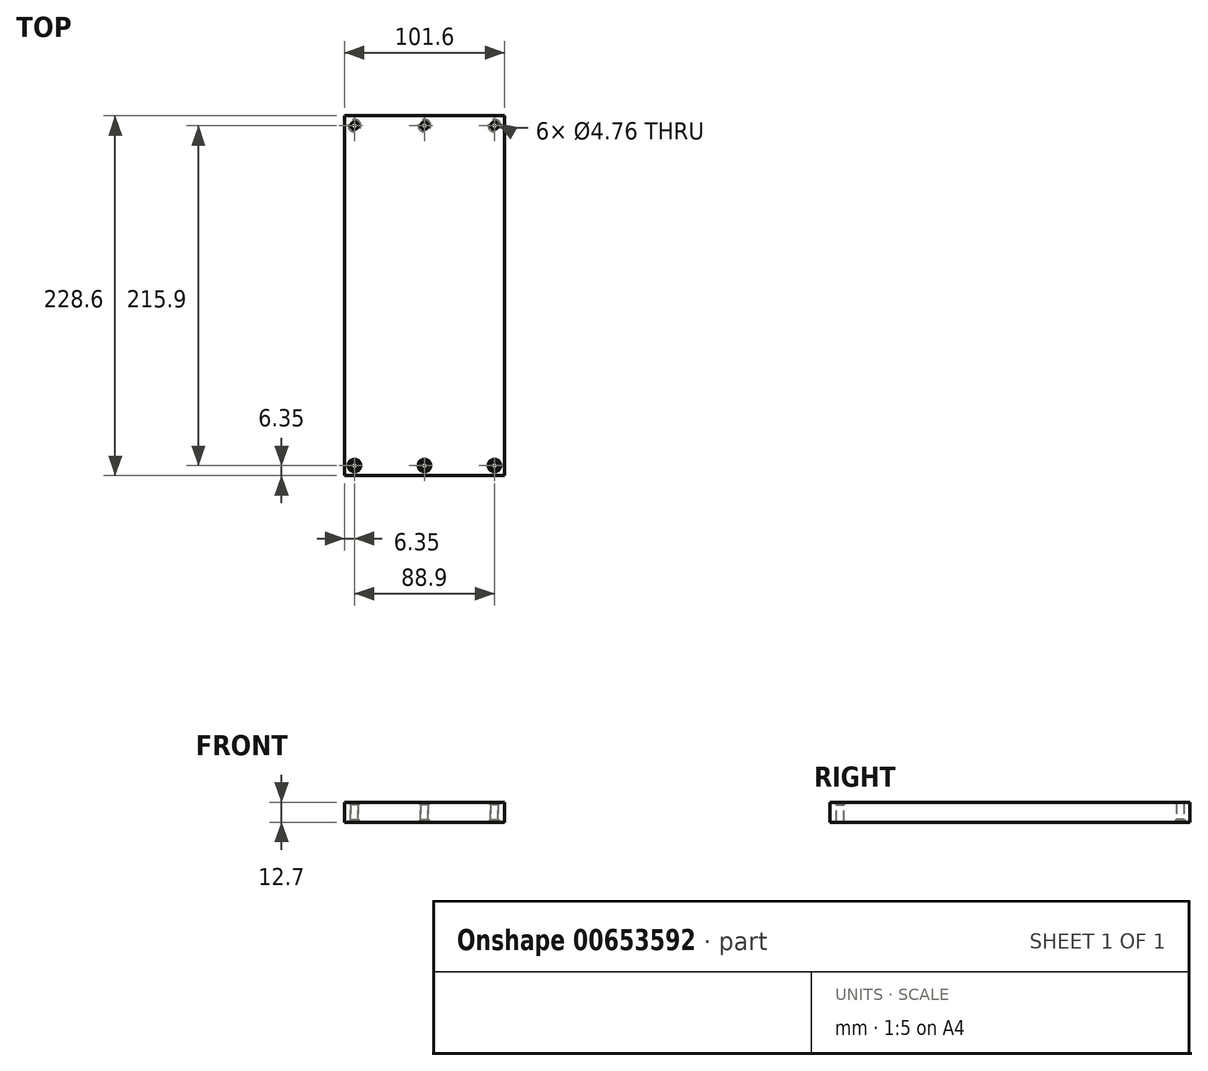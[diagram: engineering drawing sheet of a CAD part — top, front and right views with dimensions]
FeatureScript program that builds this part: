
annotation { "Feature Type Name" : "Feature", "Feature Type Description" : "" }
export const myFeature = defineFeature(function(context is Context, id is Id, definition is map)
    precondition{}
    {
        {
            var Q0;
            Q0=qCreatedBy(makeId("Top.planeOp"),FACE);
            var sketch = newSketch(context, id + "F0", { "sketchPlane" : qUnion([Q0])});
            skLineSegment(sketch, "E0.bottom", {"start": v(50.8, 114.3) * mm, "end": v(-50.8, 114.3) * mm});
            skLineSegment(sketch, "E0.top", {"start": v(50.8, -114.3) * mm, "end": v(-50.8, -114.3) * mm});
            skLineSegment(sketch, "E0.left", {"start": v(50.8, 114.3) * mm, "end": v(50.8, -114.3) * mm});
            skLineSegment(sketch, "E0.right", {"start": v(-50.8, 114.3) * mm, "end": v(-50.8, -114.3) * mm});
            skPoint(sketch, "E0.middle", {"position": v(0, 0) * mm});
            skSolve(sketch);
        }
        {
            var Q0;
            Q0=makeQuery(id+"F0.imprint","IMPRINT",FACE,{"disambiguationData":[TD([[makeQuery(id+"F0.imprint","IMPRINT",EDGE,{"derivedFrom":sQuery(id+"F0.wireOp",EDGE,"E0.bottom")}),1.0]])]});
            extrude(context, id + "F1", {"entities" : qUnion([Q0]), "depth" : 12.7 * mm, "offsetDistance" : 25.4 * mm});
        }
        {
            var Q0;
            Q0=makeQuery(id+"F1.opExtrude","CAP_FACE",FACE,{"disambiguationData":[OSD([sQuery(id+"F0.wireOp",EDGE,"E0.bottom"),sQuery(id+"F0.wireOp",EDGE,"E0.top"),sQuery(id+"F0.wireOp",EDGE,"E0.left"),sQuery(id+"F0.wireOp",EDGE,"E0.right")])],"isStart":false});
            var sketch = newSketch(context, id + "F2", { "sketchPlane" : qUnion([Q0])});
            skLineSegment(sketch, "E1.0", {"start": v(-44.45, -107.95) * mm, "end": v(44.45, -107.95) * mm});
            skLineSegment(sketch, "E1.1", {"start": v(-44.45, 107.95) * mm, "end": v(-44.45, -107.95) * mm});
            skLineSegment(sketch, "E1.2", {"start": v(44.45, 107.95) * mm, "end": v(-44.45, 107.95) * mm});
            skLineSegment(sketch, "E1.3", {"start": v(44.45, -107.95) * mm, "end": v(44.45, 107.95) * mm});
            skLineSegment(sketch, "E2", {"start": v(-44.45, -95.25) * mm, "end": v(44.45, -95.25) * mm});
            skLineSegment(sketch, "E3", {"start": v(44.45, 95.25) * mm, "end": v(-44.45, 95.25) * mm});
            skLineSegment(sketch, "E4", {"start": v(76.94, 0) * mm, "end": v(-80.05, 0) * mm, "construction": true});
            skPoint(sketch, "E5", {"position": v(0, 107.95) * mm});
            skPoint(sketch, "E6", {"position": v(14.82, 95.25) * mm});
            skPoint(sketch, "E7", {"position": v(-14.82, 95.25) * mm});
            skPoint(sketch, "E8", {"position": v(0, -107.95) * mm});
            skPoint(sketch, "E9", {"position": v(14.82, -95.25) * mm});
            skPoint(sketch, "E10", {"position": v(-14.82, -95.25) * mm});
            skLineSegment(sketch, "E11", {"start": v(-44.45, 95.25) * mm, "end": v(-14.82, 95.25) * mm, "construction": true});
            skLineSegment(sketch, "E12", {"start": v(-14.82, 95.25) * mm, "end": v(14.82, 95.25) * mm, "construction": true});
            skLineSegment(sketch, "E13", {"start": v(14.82, 95.25) * mm, "end": v(44.45, 95.25) * mm, "construction": true});
            skSolve(sketch);
        }
        {
            var Q0;
            Q0=sQuery(id+"F2.wireOp",VERTEX,"E1.1.end");
            var Q1;
            Q1=sQuery(id+"F2.wireOp",VERTEX,"E8");
            var Q2;
            Q2=sQuery(id+"F2.wireOp",VERTEX,"E1.3.start");
            var Q3;
            Q3=makeQuery(id+"F1.opExtrude","SWEPT_BODY",BODY,{"disambiguationData":[OSD([sQuery(id+"F0.wireOp",EDGE,"E0.bottom"),sQuery(id+"F0.wireOp",EDGE,"E0.top"),sQuery(id+"F0.wireOp",EDGE,"E0.left"),sQuery(id+"F0.wireOp",EDGE,"E0.right")])]});
            hole(context, id + "F3", {"style" : HoleStyle.C_SINK, "endStyle" : HoleEndStyle.THROUGH, "holeDiameter" : 4.76 * mm, "cSinkDiameter" : 7.94 * mm, "cSinkAngle" : 85 * degree, "majorDiameter" : 6.35 * mm, "isTappedThrough" : true, "tappedDepth" : 12.7 * mm, "tapClearance" : 3, "locations" : qUnion([Q0, Q1, Q2]), "scope" : qUnion([Q3])});
        }
        {
            var Q0;
            Q0=makeQuery(id+"F1.opExtrude","CAP_FACE",FACE,{"disambiguationData":[OSD([sQuery(id+"F0.wireOp",EDGE,"E0.bottom"),sQuery(id+"F0.wireOp",EDGE,"E0.top"),sQuery(id+"F0.wireOp",EDGE,"E0.left"),sQuery(id+"F0.wireOp",EDGE,"E0.right")])],"isStart":true});
            var sketch = newSketch(context, id + "F4", { "sketchPlane" : qUnion([Q0])});
            skLineSegment(sketch, "E14.0", {"start": v(44.45, 107.95) * mm, "end": v(-44.45, 107.95) * mm});
            skLineSegment(sketch, "E14.1", {"start": v(44.45, -107.95) * mm, "end": v(44.45, 107.95) * mm});
            skLineSegment(sketch, "E14.2", {"start": v(-44.45, -107.95) * mm, "end": v(44.45, -107.95) * mm});
            skLineSegment(sketch, "E14.3", {"start": v(-44.45, 107.95) * mm, "end": v(-44.45, -107.95) * mm});
            skPoint(sketch, "E15", {"position": v(0, -107.95) * mm});
            skSolve(sketch);
        }
        {
            var Q0;
            Q0=sQuery(id+"F4.wireOp",VERTEX,"E14.1.start");
            var Q1;
            Q1=sQuery(id+"F4.wireOp",VERTEX,"E15");
            var Q2;
            Q2=sQuery(id+"F4.wireOp",VERTEX,"E14.3.end");
            var Q3;
            Q3=makeQuery(id+"F1.opExtrude","SWEPT_BODY",BODY,{"disambiguationData":[OSD([sQuery(id+"F0.wireOp",EDGE,"E0.bottom"),sQuery(id+"F0.wireOp",EDGE,"E0.top"),sQuery(id+"F0.wireOp",EDGE,"E0.left"),sQuery(id+"F0.wireOp",EDGE,"E0.right")])]});
            hole(context, id + "F5", {"style" : HoleStyle.C_SINK, "endStyle" : HoleEndStyle.THROUGH, "holeDiameter" : 4.76 * mm, "cSinkDiameter" : 7.94 * mm, "cSinkAngle" : 85 * degree, "majorDiameter" : 6.35 * mm, "isTappedThrough" : true, "tappedDepth" : 12.7 * mm, "tapClearance" : 3, "locations" : qUnion([Q0, Q1, Q2]), "scope" : qUnion([Q3])});
        }
    });
